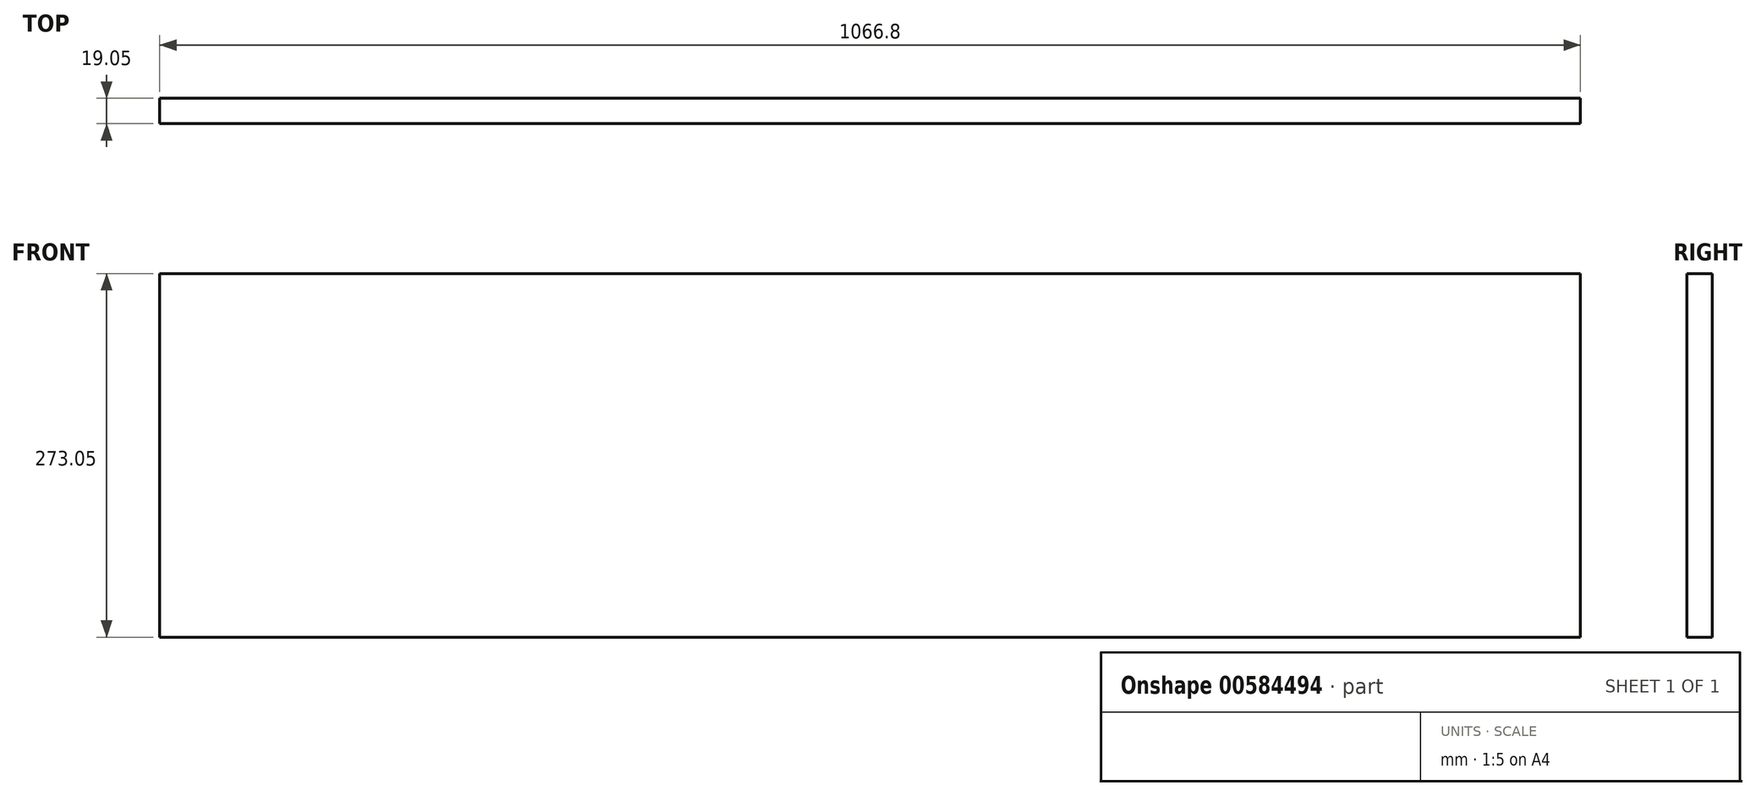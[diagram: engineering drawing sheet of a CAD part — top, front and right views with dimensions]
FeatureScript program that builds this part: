
annotation { "Feature Type Name" : "Feature", "Feature Type Description" : "" }
export const myFeature = defineFeature(function(context is Context, id is Id, definition is map)
    precondition{}
    {
        {
            var Q0;
            Q0=qCreatedBy(makeId("Front.planeOp"),FACE);
            var sketch = newSketch(context, id + "F0", { "sketchPlane" : qUnion([Q0])});
            skLineSegment(sketch, "E0.bottom", {"start": v(0, 0) * mm, "end": v(1066.8, 0) * mm});
            skLineSegment(sketch, "E0.top", {"start": v(0, 273.05) * mm, "end": v(1066.8, 273.05) * mm});
            skLineSegment(sketch, "E0.left", {"start": v(0, 0) * mm, "end": v(0, 273.05) * mm});
            skLineSegment(sketch, "E0.right", {"start": v(1066.8, 0) * mm, "end": v(1066.8, 273.05) * mm});
            skSolve(sketch);
        }
        {
            var Q0;
            Q0=makeQuery(id+"F0.imprint","IMPRINT",FACE,{"disambiguationData":[TD([[makeQuery(id+"F0.imprint","IMPRINT",EDGE,{"derivedFrom":sQuery(id+"F0.wireOp",EDGE,"E0.bottom")}),1.0]])]});
            extrude(context, id + "F1", {"entities" : qUnion([Q0]), "depth" : 19.05 * mm, "offsetDistance" : 25.4 * mm});
        }
    });
